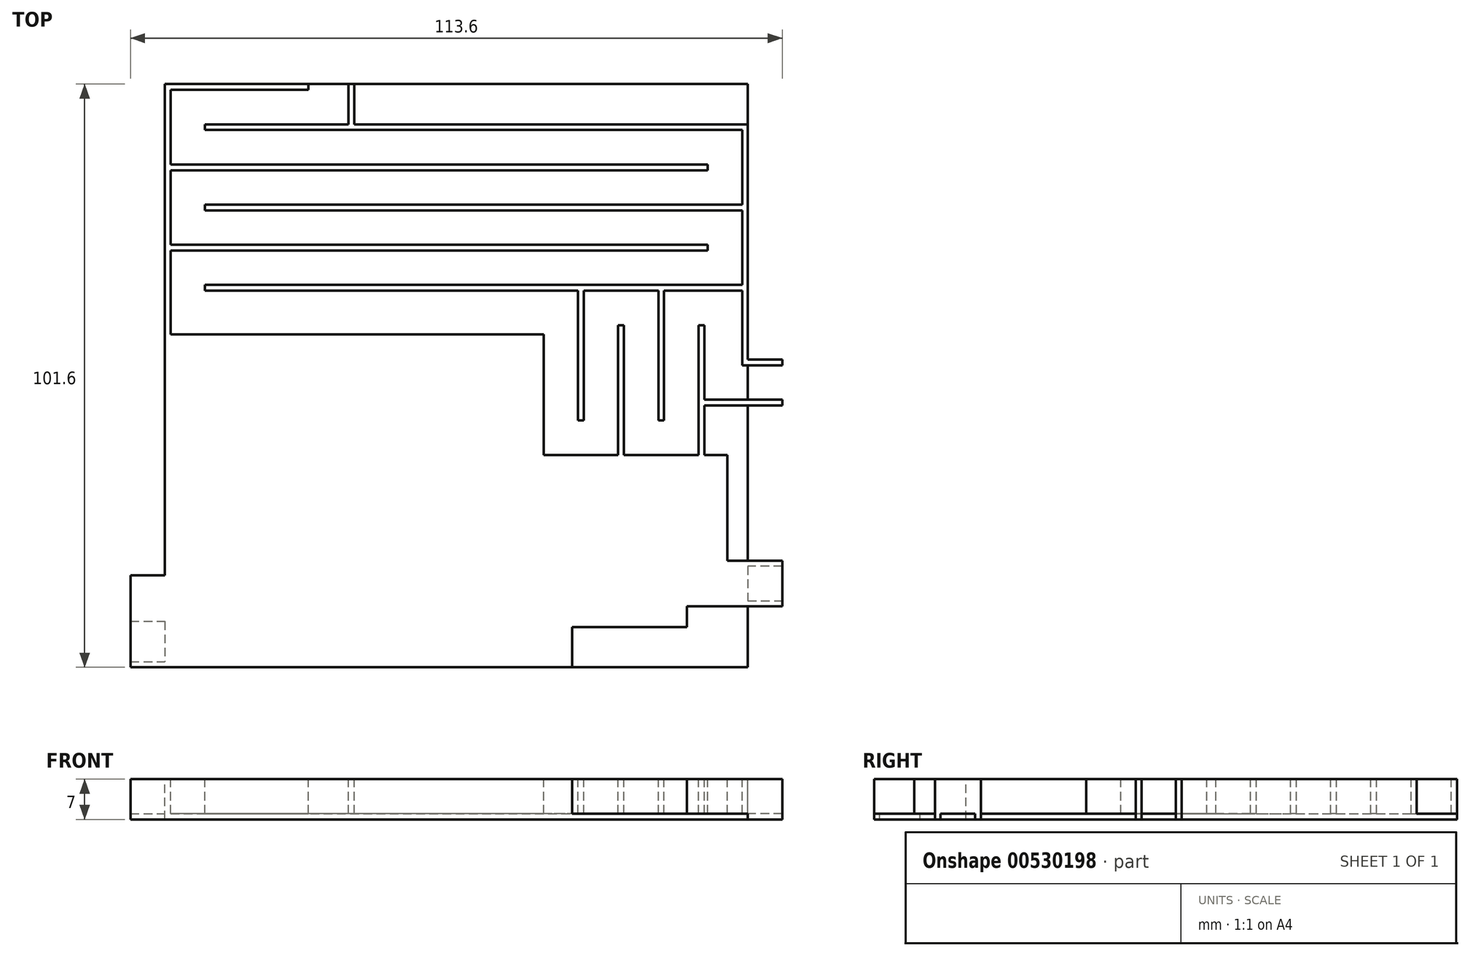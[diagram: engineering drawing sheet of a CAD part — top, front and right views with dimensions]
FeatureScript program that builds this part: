
annotation { "Feature Type Name" : "Feature", "Feature Type Description" : "" }
export const myFeature = defineFeature(function(context is Context, id is Id, definition is map)
    precondition{}
    {
        {
            var Q0;
            Q0=qCreatedBy(makeId("Top.planeOp"),FACE);
            var sketch = newSketch(context, id + "F0", { "sketchPlane" : qUnion([Q0])});
            skLineSegment(sketch, "E0.bottom", {"start": v(56.8, 50.8) * mm, "end": v(-56.8, 50.8) * mm});
            skLineSegment(sketch, "E0.top", {"start": v(56.8, -50.8) * mm, "end": v(-56.8, -50.8) * mm});
            skLineSegment(sketch, "E0.left", {"start": v(56.8, 50.8) * mm, "end": v(56.8, -50.8) * mm});
            skLineSegment(sketch, "E0.right", {"start": v(-56.8, 50.8) * mm, "end": v(-56.8, -50.8) * mm});
            skPoint(sketch, "E0.middle", {"position": v(0, 0) * mm});
            skSolve(sketch);
        }
        {
            var Q0;
            Q0=makeQuery(id+"F0.imprint","IMPRINT",FACE,{"disambiguationData":[TD([[makeQuery(id+"F0.imprint","IMPRINT",EDGE,{"derivedFrom":sQuery(id+"F0.wireOp",EDGE,"E0.bottom")}),1.0]])]});
            extrude(context, id + "F1", {"entities" : qUnion([Q0]), "depth" : 7 * mm, "offsetDistance" : 25.4 * mm});
        }
        {
            var Q0;
            Q0=makeQuery(id+"F1.opExtrude","CAP_FACE",FACE,{"disambiguationData":[OSD([sQuery(id+"F0.wireOp",EDGE,"E0.bottom"),sQuery(id+"F0.wireOp",EDGE,"E0.top"),sQuery(id+"F0.wireOp",EDGE,"E0.left"),sQuery(id+"F0.wireOp",EDGE,"E0.right")])],"isStart":false});
            var sketch = newSketch(context, id + "F2", { "sketchPlane" : qUnion([Q0])});
            skPoint(sketch, "E1", {"position": v(-56.8, -42.8) * mm});
            skPoint(sketch, "E2", {"position": v(-10.8, -41.8) * mm});
            skLineSegment(sketch, "E3.bottom", {"start": v(-56.8, -42.8) * mm, "end": v(-10.8, -42.8) * mm});
            skLineSegment(sketch, "E3.top", {"start": v(-56.8, -41.8) * mm, "end": v(-10.8, -41.8) * mm});
            skLineSegment(sketch, "E3.left", {"start": v(-56.8, -42.8) * mm, "end": v(-56.8, -41.8) * mm});
            skLineSegment(sketch, "E3.right", {"start": v(-10.8, -42.8) * mm, "end": v(-10.8, -41.8) * mm});
            skPoint(sketch, "E4", {"position": v(-56.8, -35.8) * mm});
            skPoint(sketch, "E5", {"position": v(-49.8, -34.8) * mm});
            skLineSegment(sketch, "E6.bottom", {"start": v(-56.8, -35.8) * mm, "end": v(-49.8, -35.8) * mm});
            skLineSegment(sketch, "E6.top", {"start": v(-56.8, -34.8) * mm, "end": v(-49.8, -34.8) * mm});
            skLineSegment(sketch, "E6.left", {"start": v(-56.8, -35.8) * mm, "end": v(-56.8, -34.8) * mm});
            skLineSegment(sketch, "E6.right", {"start": v(-49.8, -35.8) * mm, "end": v(-49.8, -34.8) * mm});
            skPoint(sketch, "E7", {"position": v(-50.8, 7.2) * mm});
            skLineSegment(sketch, "E8.bottom", {"start": v(-50.8, 7.2) * mm, "end": v(-49.8, 7.2) * mm});
            skLineSegment(sketch, "E8.top", {"start": v(-50.8, -34.8) * mm, "end": v(-49.8, -34.8) * mm});
            skLineSegment(sketch, "E8.left", {"start": v(-50.8, 7.2) * mm, "end": v(-50.8, -34.8) * mm});
            skLineSegment(sketch, "E8.right", {"start": v(-49.8, 7.2) * mm, "end": v(-49.8, -34.8) * mm});
            skPoint(sketch, "E9", {"position": v(-11.8, -13.8) * mm});
            skLineSegment(sketch, "E10.bottom", {"start": v(-11.8, -13.8) * mm, "end": v(-10.8, -13.8) * mm});
            skLineSegment(sketch, "E10.top", {"start": v(-11.8, -41.8) * mm, "end": v(-10.8, -41.8) * mm});
            skLineSegment(sketch, "E10.left", {"start": v(-11.8, -13.8) * mm, "end": v(-11.8, -41.8) * mm});
            skLineSegment(sketch, "E10.right", {"start": v(-10.8, -13.8) * mm, "end": v(-10.8, -41.8) * mm});
            skPoint(sketch, "E11", {"position": v(-17.8, -35.8) * mm});
            skLineSegment(sketch, "E12.bottom", {"start": v(-17.8, -35.8) * mm, "end": v(-49.8, -35.8) * mm});
            skLineSegment(sketch, "E12.top", {"start": v(-17.8, -34.8) * mm, "end": v(-49.8, -34.8) * mm});
            skLineSegment(sketch, "E12.left", {"start": v(-17.8, -35.8) * mm, "end": v(-17.8, -34.8) * mm});
            skPoint(sketch, "E13", {"position": v(-43.8, -28.8) * mm});
            skPoint(sketch, "E14", {"position": v(-11.8, -27.8) * mm});
            skLineSegment(sketch, "E15.bottom", {"start": v(-43.8, -28.8) * mm, "end": v(-11.8, -28.8) * mm});
            skLineSegment(sketch, "E15.top", {"start": v(-43.8, -27.8) * mm, "end": v(-11.8, -27.8) * mm});
            skLineSegment(sketch, "E15.left", {"start": v(-43.8, -28.8) * mm, "end": v(-43.8, -27.8) * mm});
            skLineSegment(sketch, "E15.right", {"start": v(-11.8, -28.8) * mm, "end": v(-11.8, -27.8) * mm});
            skPoint(sketch, "E16", {"position": v(-17.8, -21.8) * mm});
            skPoint(sketch, "E17", {"position": v(-49.8, -20.8) * mm});
            skLineSegment(sketch, "E18.bottom", {"start": v(-49.8, -20.8) * mm, "end": v(-17.8, -20.8) * mm});
            skLineSegment(sketch, "E18.top", {"start": v(-49.8, -21.8) * mm, "end": v(-17.8, -21.8) * mm});
            skLineSegment(sketch, "E18.left", {"start": v(-49.8, -20.8) * mm, "end": v(-49.8, -21.8) * mm});
            skLineSegment(sketch, "E18.right", {"start": v(-17.8, -20.8) * mm, "end": v(-17.8, -21.8) * mm});
            skPoint(sketch, "E19", {"position": v(-43.8, -14.8) * mm});
            skLineSegment(sketch, "E20.bottom", {"start": v(-43.8, -14.8) * mm, "end": v(-11.8, -14.8) * mm});
            skLineSegment(sketch, "E20.top", {"start": v(-43.8, -13.8) * mm, "end": v(-11.8, -13.8) * mm});
            skLineSegment(sketch, "E20.left", {"start": v(-43.8, -14.8) * mm, "end": v(-43.8, -13.8) * mm});
            skLineSegment(sketch, "E20.right", {"start": v(-11.8, -14.8) * mm, "end": v(-11.8, -13.8) * mm});
            skPoint(sketch, "E21", {"position": v(-17.8, -7.8) * mm});
            skPoint(sketch, "E22", {"position": v(-49.8, -6.8) * mm});
            skLineSegment(sketch, "E23.bottom", {"start": v(-49.8, -6.8) * mm, "end": v(-17.8, -6.8) * mm});
            skLineSegment(sketch, "E23.top", {"start": v(-49.8, -7.8) * mm, "end": v(-17.8, -7.8) * mm});
            skLineSegment(sketch, "E23.left", {"start": v(-49.8, -6.8) * mm, "end": v(-49.8, -7.8) * mm});
            skLineSegment(sketch, "E23.right", {"start": v(-17.8, -6.8) * mm, "end": v(-17.8, -7.8) * mm});
            skPoint(sketch, "E24", {"position": v(-10.8, -7.8) * mm});
            skPoint(sketch, "E25", {"position": v(-11.8, 0.2) * mm});
            skLineSegment(sketch, "E26.bottom", {"start": v(-11.8, 0.2) * mm, "end": v(-10.8, 0.2) * mm});
            skLineSegment(sketch, "E26.top", {"start": v(-11.8, -7.8) * mm, "end": v(-10.8, -7.8) * mm});
            skPoint(sketch, "E27", {"position": v(-43.8, -0.8) * mm});
            skLineSegment(sketch, "E28.bottom", {"start": v(-43.8, -0.8) * mm, "end": v(-10.8, -0.8) * mm});
            skLineSegment(sketch, "E28.top", {"start": v(-43.8, 0.2) * mm, "end": v(-10.8, 0.2) * mm});
            skLineSegment(sketch, "E28.left", {"start": v(-43.8, -0.8) * mm, "end": v(-43.8, 0.2) * mm});
            skLineSegment(sketch, "E28.right", {"start": v(-10.8, -0.8) * mm, "end": v(-10.8, 0.2) * mm});
            skPoint(sketch, "E29", {"position": v(14.2, 6.2) * mm});
            skLineSegment(sketch, "E30.bottom", {"start": v(-49.8, 7.2) * mm, "end": v(14.2, 7.2) * mm});
            skLineSegment(sketch, "E30.top", {"start": v(-49.8, 6.2) * mm, "end": v(14.2, 6.2) * mm});
            skLineSegment(sketch, "E30.left", {"start": v(-49.8, 7.2) * mm, "end": v(-49.8, 6.2) * mm});
            skLineSegment(sketch, "E30.right", {"start": v(14.2, 7.2) * mm, "end": v(14.2, 6.2) * mm});
            skPoint(sketch, "E31", {"position": v(8.2, 0.2) * mm});
            skLineSegment(sketch, "E32.bottom", {"start": v(8.2, 0.2) * mm, "end": v(-10.8, 0.2) * mm});
            skLineSegment(sketch, "E32.top", {"start": v(8.2, -0.8) * mm, "end": v(-10.8, -0.8) * mm});
            skLineSegment(sketch, "E32.left", {"start": v(8.2, 0.2) * mm, "end": v(8.2, -0.8) * mm});
            skLineSegment(sketch, "E32.right", {"start": v(-10.8, 0.2) * mm, "end": v(-10.8, -0.8) * mm});
            skPoint(sketch, "E33", {"position": v(15.2, -14.8) * mm});
            skLineSegment(sketch, "E34.bottom", {"start": v(15.2, -14.8) * mm, "end": v(14.2, -14.8) * mm});
            skLineSegment(sketch, "E34.top", {"start": v(15.2, 7.2) * mm, "end": v(14.2, 7.2) * mm});
            skLineSegment(sketch, "E34.left", {"start": v(15.2, -14.8) * mm, "end": v(15.2, 7.2) * mm});
            skLineSegment(sketch, "E34.right", {"start": v(14.2, -14.8) * mm, "end": v(14.2, 7.2) * mm});
            skPoint(sketch, "E35", {"position": v(7.2, -21.8) * mm});
            skLineSegment(sketch, "E36.bottom", {"start": v(7.2, -21.8) * mm, "end": v(8.2, -21.8) * mm});
            skLineSegment(sketch, "E36.top", {"start": v(7.2, 0.2) * mm, "end": v(8.2, 0.2) * mm});
            skLineSegment(sketch, "E36.left", {"start": v(7.2, -21.8) * mm, "end": v(7.2, 0.2) * mm});
            skLineSegment(sketch, "E36.right", {"start": v(8.2, -21.8) * mm, "end": v(8.2, 0.2) * mm});
            skPoint(sketch, "E37", {"position": v(39.2, -13.8) * mm});
            skLineSegment(sketch, "E38.bottom", {"start": v(15.2, -14.8) * mm, "end": v(39.2, -14.8) * mm});
            skLineSegment(sketch, "E38.top", {"start": v(15.2, -13.8) * mm, "end": v(39.2, -13.8) * mm});
            skLineSegment(sketch, "E38.left", {"start": v(15.2, -14.8) * mm, "end": v(15.2, -13.8) * mm});
            skLineSegment(sketch, "E38.right", {"start": v(39.2, -14.8) * mm, "end": v(39.2, -13.8) * mm});
            skPoint(sketch, "E39", {"position": v(40.2, -43.8) * mm});
            skLineSegment(sketch, "E40.bottom", {"start": v(40.2, -43.8) * mm, "end": v(39.2, -43.8) * mm});
            skLineSegment(sketch, "E40.top", {"start": v(40.2, -14.8) * mm, "end": v(39.2, -14.8) * mm});
            skLineSegment(sketch, "E40.left", {"start": v(40.2, -43.8) * mm, "end": v(40.2, -14.8) * mm});
            skLineSegment(sketch, "E40.right", {"start": v(39.2, -43.8) * mm, "end": v(39.2, -14.8) * mm});
            skLineSegment(sketch, "E41.top", {"start": v(40.2, -13.8) * mm, "end": v(39.2, -13.8) * mm});
            skLineSegment(sketch, "E41.left", {"start": v(40.2, -43.8) * mm, "end": v(40.2, -13.8) * mm});
            skLineSegment(sketch, "E41.right", {"start": v(39.2, -43.8) * mm, "end": v(39.2, -13.8) * mm});
            skPoint(sketch, "E42", {"position": v(20.2, -42.8) * mm});
            skLineSegment(sketch, "E43.bottom", {"start": v(20.2, -42.8) * mm, "end": v(40.2, -42.8) * mm});
            skLineSegment(sketch, "E43.top", {"start": v(20.2, -43.8) * mm, "end": v(40.2, -43.8) * mm});
            skLineSegment(sketch, "E43.left", {"start": v(20.2, -42.8) * mm, "end": v(20.2, -43.8) * mm});
            skLineSegment(sketch, "E43.right", {"start": v(40.2, -42.8) * mm, "end": v(40.2, -43.8) * mm});
            skPoint(sketch, "E44", {"position": v(19.2, -50.8) * mm});
            skLineSegment(sketch, "E45.bottom", {"start": v(19.2, -50.8) * mm, "end": v(20.2, -50.8) * mm});
            skLineSegment(sketch, "E45.top", {"start": v(19.2, -42.8) * mm, "end": v(20.2, -42.8) * mm});
            skLineSegment(sketch, "E45.left", {"start": v(19.2, -50.8) * mm, "end": v(19.2, -42.8) * mm});
            skLineSegment(sketch, "E45.right", {"start": v(20.2, -50.8) * mm, "end": v(20.2, -42.8) * mm});
            skPoint(sketch, "E46", {"position": v(33.2, -20.8) * mm});
            skLineSegment(sketch, "E47.bottom", {"start": v(33.2, -20.8) * mm, "end": v(8.2, -20.8) * mm});
            skLineSegment(sketch, "E47.top", {"start": v(33.2, -21.8) * mm, "end": v(8.2, -21.8) * mm});
            skLineSegment(sketch, "E47.left", {"start": v(33.2, -20.8) * mm, "end": v(33.2, -21.8) * mm});
            skLineSegment(sketch, "E47.right", {"start": v(8.2, -20.8) * mm, "end": v(8.2, -21.8) * mm});
            skPoint(sketch, "E48", {"position": v(32.2, -36.8) * mm});
            skLineSegment(sketch, "E49.bottom", {"start": v(32.2, -36.8) * mm, "end": v(33.2, -36.8) * mm});
            skLineSegment(sketch, "E49.top", {"start": v(32.2, -21.8) * mm, "end": v(33.2, -21.8) * mm});
            skLineSegment(sketch, "E49.left", {"start": v(32.2, -36.8) * mm, "end": v(32.2, -21.8) * mm});
            skLineSegment(sketch, "E49.right", {"start": v(33.2, -36.8) * mm, "end": v(33.2, -21.8) * mm});
            skPoint(sketch, "E50", {"position": v(13.2, -35.8) * mm});
            skLineSegment(sketch, "E51.bottom", {"start": v(13.2, -35.8) * mm, "end": v(32.2, -35.8) * mm});
            skLineSegment(sketch, "E51.top", {"start": v(13.2, -36.8) * mm, "end": v(32.2, -36.8) * mm});
            skLineSegment(sketch, "E51.left", {"start": v(13.2, -35.8) * mm, "end": v(13.2, -36.8) * mm});
            skLineSegment(sketch, "E51.right", {"start": v(32.2, -35.8) * mm, "end": v(32.2, -36.8) * mm});
            skPoint(sketch, "E52", {"position": v(12.2, -50.8) * mm});
            skLineSegment(sketch, "E53.bottom", {"start": v(12.2, -50.8) * mm, "end": v(13.2, -50.8) * mm});
            skLineSegment(sketch, "E53.top", {"start": v(12.2, -35.8) * mm, "end": v(13.2, -35.8) * mm});
            skLineSegment(sketch, "E53.left", {"start": v(12.2, -50.8) * mm, "end": v(12.2, -35.8) * mm});
            skLineSegment(sketch, "E53.right", {"start": v(13.2, -50.8) * mm, "end": v(13.2, -35.8) * mm});
            skLineSegment(sketch, "E54.bottom", {"start": v(-10.8, -7.8) * mm, "end": v(-11.8, -7.8) * mm});
            skLineSegment(sketch, "E54.top", {"start": v(-10.8, -13.8) * mm, "end": v(-11.8, -13.8) * mm});
            skLineSegment(sketch, "E54.left", {"start": v(-10.8, -7.8) * mm, "end": v(-10.8, -13.8) * mm});
            skLineSegment(sketch, "E54.right", {"start": v(-11.8, -7.8) * mm, "end": v(-11.8, -13.8) * mm});
            skPoint(sketch, "E55", {"position": v(1.2, -6.8) * mm});
            skLineSegment(sketch, "E56.bottom", {"start": v(1.2, -6.8) * mm, "end": v(-11.8, -6.8) * mm});
            skLineSegment(sketch, "E56.top", {"start": v(1.2, -7.8) * mm, "end": v(-11.8, -7.8) * mm});
            skLineSegment(sketch, "E56.left", {"start": v(1.2, -6.8) * mm, "end": v(1.2, -7.8) * mm});
            skLineSegment(sketch, "E56.right", {"start": v(-11.8, -6.8) * mm, "end": v(-11.8, -7.8) * mm});
            skPoint(sketch, "E57", {"position": v(-4.8, -13.8) * mm});
            skPoint(sketch, "E58", {"position": v(7.2, -14.8) * mm});
            skLineSegment(sketch, "E59.bottom", {"start": v(-4.8, -13.8) * mm, "end": v(7.2, -13.8) * mm});
            skLineSegment(sketch, "E59.top", {"start": v(-4.8, -14.8) * mm, "end": v(7.2, -14.8) * mm});
            skLineSegment(sketch, "E59.left", {"start": v(-4.8, -13.8) * mm, "end": v(-4.8, -14.8) * mm});
            skLineSegment(sketch, "E59.right", {"start": v(7.2, -13.8) * mm, "end": v(7.2, -14.8) * mm});
            skPoint(sketch, "E60", {"position": v(-10.8, -20.8) * mm});
            skPoint(sketch, "E61", {"position": v(1.2, -21.8) * mm});
            skLineSegment(sketch, "E62.bottom", {"start": v(-10.8, -20.8) * mm, "end": v(1.2, -20.8) * mm});
            skLineSegment(sketch, "E62.top", {"start": v(-10.8, -21.8) * mm, "end": v(1.2, -21.8) * mm});
            skLineSegment(sketch, "E62.left", {"start": v(-10.8, -20.8) * mm, "end": v(-10.8, -21.8) * mm});
            skLineSegment(sketch, "E62.right", {"start": v(1.2, -20.8) * mm, "end": v(1.2, -21.8) * mm});
            skPoint(sketch, "E63", {"position": v(26.2, -28.8) * mm});
            skLineSegment(sketch, "E64.bottom", {"start": v(26.2, -28.8) * mm, "end": v(-11.8, -28.8) * mm});
            skLineSegment(sketch, "E64.top", {"start": v(26.2, -27.8) * mm, "end": v(-11.8, -27.8) * mm});
            skLineSegment(sketch, "E64.left", {"start": v(26.2, -28.8) * mm, "end": v(26.2, -27.8) * mm});
            skPoint(sketch, "E65", {"position": v(-4.8, -36.8) * mm});
            skLineSegment(sketch, "E66.bottom", {"start": v(-4.8, -36.8) * mm, "end": v(13.2, -36.8) * mm});
            skLineSegment(sketch, "E66.top", {"start": v(-4.8, -35.8) * mm, "end": v(13.2, -35.8) * mm});
            skLineSegment(sketch, "E66.left", {"start": v(-4.8, -36.8) * mm, "end": v(-4.8, -35.8) * mm});
            skLineSegment(sketch, "E66.right", {"start": v(13.2, -36.8) * mm, "end": v(13.2, -35.8) * mm});
            skPoint(sketch, "E67", {"position": v(6.2, -41.8) * mm});
            skPoint(sketch, "E68", {"position": v(5.2, -50.8) * mm});
            skLineSegment(sketch, "E69.bottom", {"start": v(6.2, -41.8) * mm, "end": v(5.2, -41.8) * mm});
            skLineSegment(sketch, "E69.top", {"start": v(6.2, -50.8) * mm, "end": v(5.2, -50.8) * mm});
            skLineSegment(sketch, "E69.left", {"start": v(6.2, -41.8) * mm, "end": v(6.2, -50.8) * mm});
            skLineSegment(sketch, "E69.right", {"start": v(5.2, -41.8) * mm, "end": v(5.2, -50.8) * mm});
            skPoint(sketch, "E70", {"position": v(-0.8, -42.8) * mm});
            skLineSegment(sketch, "E71.bottom", {"start": v(-0.8, -42.8) * mm, "end": v(-10.8, -42.8) * mm});
            skLineSegment(sketch, "E71.top", {"start": v(-0.8, -41.8) * mm, "end": v(-10.8, -41.8) * mm});
            skLineSegment(sketch, "E71.left", {"start": v(-0.8, -42.8) * mm, "end": v(-0.8, -41.8) * mm});
            skPoint(sketch, "E72", {"position": v(-0.8, -50.8) * mm});
            skPoint(sketch, "E72.positionSnap0", {"position": v(0, -50.8) * mm});
            skPoint(sketch, "E73", {"position": v(-1.8, -48.8) * mm});
            skLineSegment(sketch, "E74.bottom", {"start": v(-1.8, -48.8) * mm, "end": v(-0.8, -48.8) * mm});
            skLineSegment(sketch, "E74.top", {"start": v(-1.8, -50.8) * mm, "end": v(-0.8, -50.8) * mm});
            skLineSegment(sketch, "E74.left", {"start": v(-1.8, -48.8) * mm, "end": v(-1.8, -50.8) * mm});
            skLineSegment(sketch, "E74.right", {"start": v(-0.8, -48.8) * mm, "end": v(-0.8, -50.8) * mm});
            skPoint(sketch, "E75", {"position": v(-56.8, -49.8) * mm});
            skLineSegment(sketch, "E76.bottom", {"start": v(-56.8, -49.8) * mm, "end": v(-1.8, -49.8) * mm});
            skLineSegment(sketch, "E76.top", {"start": v(-56.8, -48.8) * mm, "end": v(-1.8, -48.8) * mm});
            skLineSegment(sketch, "E76.left", {"start": v(-56.8, -49.8) * mm, "end": v(-56.8, -48.8) * mm});
            skLineSegment(sketch, "E76.right", {"start": v(-1.8, -49.8) * mm, "end": v(-1.8, -48.8) * mm});
            skSolve(sketch);
        }
        {
            var Q0;
            {var subQ14=sQuery(id+"F2.wireOp",EDGE,"E3.bottom");Q0=makeQuery(id+"F2.imprint","IMPRINT",FACE,{"disambiguationData":[TD([[makeQuery(id+"F2.imprint","IMPRINT",EDGE,{"derivedFrom":subQ14}),-1.0]])]});}
            var Q1;
            {var subQ0=sQuery(id+"F2.wireOp",EDGE,"E74.left");Q1=makeQuery(id+"F2.imprint","IMPRINT",FACE,{"disambiguationData":[TD([[makeQuery(id+"F2.imprint","IMPRINT",EDGE,{"derivedFrom":subQ0}),-1.0]])]});}
            extrude(context, id + "F3", {"entities" : qUnion([Q0, Q1]), "operationType" : NewBodyOperationType.REMOVE, "oppositeDirection" : true, "depth" : 6 * mm, "offsetDistance" : 25.4 * mm});
        }
        {
            var Q0;
            {var subQ9=sQuery(id+"F0.wireOp",EDGE,"E0.bottom");var subQ10=sQuery(id+"F0.wireOp",EDGE,"E0.right");var subQ11=sQuery(id+"F0.wireOp",EDGE,"E0.top");var subQ12=sQuery(id+"F0.wireOp",EDGE,"E0.left");Q0=makeQuery(id+"F3.boolean.opBoolean","SPLIT",FACE,{"disambiguationData":[TD([makeQuery(id+"F1.opExtrude","SWEPT_FACE",FACE,{"disambiguationData":[OSD([subQ9])]})])],"derivedFrom":makeQuery(id+"F1.opExtrude","CAP_FACE",FACE,{"disambiguationData":[OSD([subQ9,subQ11,subQ12,subQ10])],"isStart":false})});}
            var sketch = newSketch(context, id + "F4", { "sketchPlane" : qUnion([Q0])});
            skPoint(sketch, "E77", {"position": v(56.8, -43.8) * mm});
            skLineSegment(sketch, "E78.left", {"start": v(19.2, -42.8) * mm, "end": v(19.2, -43.8) * mm});
            skLineSegment(sketch, "E78.right", {"start": v(56.8, -42.8) * mm, "end": v(56.8, -43.8) * mm});
            skPoint(sketch, "E79", {"position": v(20.2, -50.8) * mm});
            skLineSegment(sketch, "E80.bottom", {"start": v(20.2, -50.8) * mm, "end": v(19.2, -50.8) * mm});
            skLineSegment(sketch, "E80.top", {"start": v(20.2, -43.8) * mm, "end": v(19.2, -43.8) * mm});
            skLineSegment(sketch, "E80.left", {"start": v(20.2, -50.8) * mm, "end": v(20.2, -43.8) * mm});
            skLineSegment(sketch, "E80.right", {"start": v(19.2, -50.8) * mm, "end": v(19.2, -43.8) * mm});
            skPoint(sketch, "E81", {"position": v(56.8, -36.8) * mm});
            skPoint(sketch, "E82", {"position": v(39.2, -35.8) * mm});
            skLineSegment(sketch, "E83.left", {"start": v(39.2, -35.8) * mm, "end": v(39.2, -36.8) * mm});
            skLineSegment(sketch, "E83.right", {"start": v(56.8, -35.8) * mm, "end": v(56.8, -36.8) * mm});
            skPoint(sketch, "E84", {"position": v(56.8, -40.2) * mm});
            skPoint(sketch, "E85", {"position": v(39.2, -39.2) * mm});
            skLineSegment(sketch, "E86.bottom", {"start": v(39.2, -39.2) * mm, "end": v(56.8, -39.2) * mm});
            skLineSegment(sketch, "E86.top", {"start": v(39.2, -40.2) * mm, "end": v(56.8, -40.2) * mm});
            skLineSegment(sketch, "E86.left", {"start": v(39.2, -39.2) * mm, "end": v(39.2, -40.2) * mm});
            skLineSegment(sketch, "E86.right", {"start": v(56.8, -39.2) * mm, "end": v(56.8, -40.2) * mm});
            skPoint(sketch, "E87", {"position": v(40.2, -43.8) * mm});
            skLineSegment(sketch, "E88.bottom", {"start": v(40.2, -43.8) * mm, "end": v(19.2, -43.8) * mm});
            skLineSegment(sketch, "E88.top", {"start": v(40.2, -42.8) * mm, "end": v(19.2, -42.8) * mm});
            skLineSegment(sketch, "E88.left", {"start": v(40.2, -43.8) * mm, "end": v(40.2, -42.8) * mm});
            skLineSegment(sketch, "E88.right", {"start": v(19.2, -43.8) * mm, "end": v(19.2, -42.8) * mm});
            skLineSegment(sketch, "E89.bottom", {"start": v(40.2, -43.8) * mm, "end": v(39.2, -43.8) * mm});
            skLineSegment(sketch, "E89.top", {"start": v(40.2, -39.2) * mm, "end": v(39.2, -39.2) * mm});
            skLineSegment(sketch, "E89.left", {"start": v(40.2, -43.8) * mm, "end": v(40.2, -39.2) * mm});
            skLineSegment(sketch, "E89.right", {"start": v(39.2, -43.8) * mm, "end": v(39.2, -39.2) * mm});
            skPoint(sketch, "E90", {"position": v(56.8, -33.2) * mm});
            skPoint(sketch, "E91", {"position": v(47.2, -13.8) * mm});
            skLineSegment(sketch, "E92.bottom", {"start": v(47.2, -13.8) * mm, "end": v(14.2, -13.8) * mm});
            skLineSegment(sketch, "E92.top", {"start": v(47.2, -14.8) * mm, "end": v(14.2, -14.8) * mm});
            skLineSegment(sketch, "E92.left", {"start": v(47.2, -13.8) * mm, "end": v(47.2, -14.8) * mm});
            skLineSegment(sketch, "E92.right", {"start": v(14.2, -13.8) * mm, "end": v(14.2, -14.8) * mm});
            skPoint(sketch, "E93", {"position": v(40.2, -20.8) * mm});
            skLineSegment(sketch, "E94.bottom", {"start": v(40.2, -20.8) * mm, "end": v(39.2, -20.8) * mm});
            skLineSegment(sketch, "E94.left", {"start": v(40.2, -20.8) * mm, "end": v(40.2, -39.2) * mm});
            skLineSegment(sketch, "E94.right", {"start": v(39.2, -20.8) * mm, "end": v(39.2, -39.2) * mm});
            skPoint(sketch, "E95", {"position": v(46.2, -32.2) * mm});
            skLineSegment(sketch, "E96.bottom", {"start": v(46.2, -32.2) * mm, "end": v(47.2, -32.2) * mm});
            skLineSegment(sketch, "E96.top", {"start": v(46.2, -14.8) * mm, "end": v(47.2, -14.8) * mm});
            skLineSegment(sketch, "E96.left", {"start": v(46.2, -32.2) * mm, "end": v(46.2, -14.8) * mm});
            skLineSegment(sketch, "E96.right", {"start": v(47.2, -32.2) * mm, "end": v(47.2, -14.8) * mm});
            skLineSegment(sketch, "E97.bottom", {"start": v(56.8, -33.2) * mm, "end": v(46.2, -33.2) * mm});
            skLineSegment(sketch, "E97.top", {"start": v(56.8, -32.2) * mm, "end": v(46.2, -32.2) * mm});
            skLineSegment(sketch, "E97.left", {"start": v(56.8, -33.2) * mm, "end": v(56.8, -32.2) * mm});
            skLineSegment(sketch, "E97.right", {"start": v(46.2, -33.2) * mm, "end": v(46.2, -32.2) * mm});
            skPoint(sketch, "E98", {"position": v(56.8, -50.8) * mm});
            skSolve(sketch);
        }
        {
            var Q0;
            {var subQ12=sQuery(id+"F4.wireOp",EDGE,"E78.right");Q0=makeQuery(id+"F4.imprint","IMPRINT",FACE,{"disambiguationData":[TD([[makeQuery(id+"F4.imprint","IMPRINT",EDGE,{"derivedFrom":subQ12}),-1.0]])]});}
            var Q1;
            {var subQ7=sQuery(id+"F4.wireOp",EDGE,"E83.right");Q1=makeQuery(id+"F4.imprint","IMPRINT",FACE,{"disambiguationData":[TD([[makeQuery(id+"F4.imprint","IMPRINT",EDGE,{"derivedFrom":subQ7}),-1.0]])]});}
            extrude(context, id + "F5", {"entities" : qUnion([Q0, Q1]), "operationType" : NewBodyOperationType.REMOVE, "oppositeDirection" : true, "depth" : 6 * mm, "offsetDistance" : 25.4 * mm});
        }
        {
            var Q0;
            {var subQ16=sQuery(id+"F0.wireOp",EDGE,"E0.bottom");var subQ17=makeQuery(id+"F1.opExtrude","SWEPT_FACE",FACE,{"disambiguationData":[OSD([subQ16])]});var subQ18=sQuery(id+"F0.wireOp",EDGE,"E0.right");var subQ20=sQuery(id+"F0.wireOp",EDGE,"E0.left");var subQ30=sQuery(id+"F0.wireOp",EDGE,"E0.top");Q0=makeQuery(id+"F5.boolean.opBoolean","SPLIT",FACE,{"disambiguationData":[TD([subQ17])],"derivedFrom":makeQuery(id+"F3.boolean.opBoolean","SPLIT",FACE,{"disambiguationData":[TD([subQ17])],"derivedFrom":makeQuery(id+"F1.opExtrude","CAP_FACE",FACE,{"disambiguationData":[OSD([subQ16,subQ30,subQ20,subQ18])],"isStart":false})})});}
            var sketch = newSketch(context, id + "F6", { "sketchPlane" : qUnion([Q0])});
            skPoint(sketch, "E99", {"position": v(-25.8, 50.8) * mm});
            skPoint(sketch, "E100", {"position": v(-18.8, 50.8) * mm});
            skPoint(sketch, "E101", {"position": v(-17.8, 43.8) * mm});
            skLineSegment(sketch, "E102.bottom", {"start": v(-18.8, 50.8) * mm, "end": v(-17.8, 50.8) * mm});
            skLineSegment(sketch, "E102.top", {"start": v(-18.8, 43.8) * mm, "end": v(-17.8, 43.8) * mm});
            skLineSegment(sketch, "E102.left", {"start": v(-18.8, 50.8) * mm, "end": v(-18.8, 43.8) * mm});
            skLineSegment(sketch, "E102.right", {"start": v(-17.8, 50.8) * mm, "end": v(-17.8, 43.8) * mm});
            skPoint(sketch, "E103", {"position": v(-50.8, 49.8) * mm});
            skLineSegment(sketch, "E104.bottom", {"start": v(-50.8, 49.8) * mm, "end": v(-25.8, 49.8) * mm});
            skLineSegment(sketch, "E104.top", {"start": v(-50.8, 50.8) * mm, "end": v(-25.8, 50.8) * mm});
            skLineSegment(sketch, "E104.left", {"start": v(-50.8, 49.8) * mm, "end": v(-50.8, 50.8) * mm});
            skLineSegment(sketch, "E104.right", {"start": v(-25.8, 49.8) * mm, "end": v(-25.8, 50.8) * mm});
            skPoint(sketch, "E105", {"position": v(-49.8, 35.8) * mm});
            skLineSegment(sketch, "E106.bottom", {"start": v(-49.8, 35.8) * mm, "end": v(-50.8, 35.8) * mm});
            skLineSegment(sketch, "E106.top", {"start": v(-49.8, 49.8) * mm, "end": v(-50.8, 49.8) * mm});
            skLineSegment(sketch, "E106.left", {"start": v(-49.8, 35.8) * mm, "end": v(-49.8, 49.8) * mm});
            skLineSegment(sketch, "E106.right", {"start": v(-50.8, 35.8) * mm, "end": v(-50.8, 49.8) * mm});
            skPoint(sketch, "E107", {"position": v(-43.8, 42.8) * mm});
            skLineSegment(sketch, "E108.bottom", {"start": v(-43.8, 42.8) * mm, "end": v(-17.8, 42.8) * mm});
            skLineSegment(sketch, "E108.top", {"start": v(-43.8, 43.8) * mm, "end": v(-17.8, 43.8) * mm});
            skLineSegment(sketch, "E108.left", {"start": v(-43.8, 42.8) * mm, "end": v(-43.8, 43.8) * mm});
            skLineSegment(sketch, "E108.right", {"start": v(-17.8, 42.8) * mm, "end": v(-17.8, 43.8) * mm});
            skPoint(sketch, "E109", {"position": v(50.8, 42.8) * mm});
            skLineSegment(sketch, "E110.bottom", {"start": v(-17.8, 43.8) * mm, "end": v(50.8, 43.8) * mm});
            skLineSegment(sketch, "E110.top", {"start": v(-17.8, 42.8) * mm, "end": v(50.8, 42.8) * mm});
            skLineSegment(sketch, "E110.left", {"start": v(-17.8, 43.8) * mm, "end": v(-17.8, 42.8) * mm});
            skLineSegment(sketch, "E110.right", {"start": v(50.8, 43.8) * mm, "end": v(50.8, 42.8) * mm});
            skPoint(sketch, "E111", {"position": v(49.8, 28.8) * mm});
            skLineSegment(sketch, "E112.bottom", {"start": v(49.8, 28.8) * mm, "end": v(50.8, 28.8) * mm});
            skLineSegment(sketch, "E112.top", {"start": v(49.8, 43.8) * mm, "end": v(50.8, 43.8) * mm});
            skLineSegment(sketch, "E112.left", {"start": v(49.8, 28.8) * mm, "end": v(49.8, 43.8) * mm});
            skLineSegment(sketch, "E112.right", {"start": v(50.8, 28.8) * mm, "end": v(50.8, 43.8) * mm});
            skPoint(sketch, "E113", {"position": v(43.8, 36.8) * mm});
            skLineSegment(sketch, "E114.bottom", {"start": v(43.8, 36.8) * mm, "end": v(-49.8, 36.8) * mm});
            skLineSegment(sketch, "E114.top", {"start": v(43.8, 35.8) * mm, "end": v(-49.8, 35.8) * mm});
            skLineSegment(sketch, "E114.left", {"start": v(43.8, 36.8) * mm, "end": v(43.8, 35.8) * mm});
            skLineSegment(sketch, "E114.right", {"start": v(-49.8, 36.8) * mm, "end": v(-49.8, 35.8) * mm});
            skPoint(sketch, "E115", {"position": v(-50.8, 21.8) * mm});
            skLineSegment(sketch, "E116.bottom", {"start": v(-50.8, 21.8) * mm, "end": v(-49.8, 21.8) * mm});
            skLineSegment(sketch, "E116.top", {"start": v(-50.8, 35.8) * mm, "end": v(-49.8, 35.8) * mm});
            skLineSegment(sketch, "E116.left", {"start": v(-50.8, 21.8) * mm, "end": v(-50.8, 35.8) * mm});
            skLineSegment(sketch, "E116.right", {"start": v(-49.8, 21.8) * mm, "end": v(-49.8, 35.8) * mm});
            skPoint(sketch, "E117", {"position": v(-43.8, 29.8) * mm});
            skLineSegment(sketch, "E118.bottom", {"start": v(-43.8, 29.8) * mm, "end": v(50.8, 29.8) * mm});
            skLineSegment(sketch, "E118.top", {"start": v(-43.8, 28.8) * mm, "end": v(50.8, 28.8) * mm});
            skLineSegment(sketch, "E118.left", {"start": v(-43.8, 29.8) * mm, "end": v(-43.8, 28.8) * mm});
            skLineSegment(sketch, "E118.right", {"start": v(50.8, 29.8) * mm, "end": v(50.8, 28.8) * mm});
            skPoint(sketch, "E119", {"position": v(49.8, 14.8) * mm});
            skLineSegment(sketch, "E120.bottom", {"start": v(49.8, 14.8) * mm, "end": v(50.8, 14.8) * mm});
            skLineSegment(sketch, "E120.left", {"start": v(49.8, 14.8) * mm, "end": v(49.8, 28.8) * mm});
            skLineSegment(sketch, "E120.right", {"start": v(50.8, 14.8) * mm, "end": v(50.8, 28.8) * mm});
            skPoint(sketch, "E121", {"position": v(43.8, 22.8) * mm});
            skLineSegment(sketch, "E122.bottom", {"start": v(43.8, 22.8) * mm, "end": v(-49.8, 22.8) * mm});
            skLineSegment(sketch, "E122.top", {"start": v(43.8, 21.8) * mm, "end": v(-49.8, 21.8) * mm});
            skLineSegment(sketch, "E122.left", {"start": v(43.8, 22.8) * mm, "end": v(43.8, 21.8) * mm});
            skLineSegment(sketch, "E122.right", {"start": v(-49.8, 22.8) * mm, "end": v(-49.8, 21.8) * mm});
            skPoint(sketch, "E123", {"position": v(-49.8, 7.8) * mm});
            skLineSegment(sketch, "E124.bottom", {"start": v(-49.8, 7.8) * mm, "end": v(-50.8, 7.8) * mm});
            skLineSegment(sketch, "E124.top", {"start": v(-49.8, 21.8) * mm, "end": v(-50.8, 21.8) * mm});
            skLineSegment(sketch, "E124.left", {"start": v(-49.8, 7.8) * mm, "end": v(-49.8, 21.8) * mm});
            skLineSegment(sketch, "E124.right", {"start": v(-50.8, 7.8) * mm, "end": v(-50.8, 21.8) * mm});
            skPoint(sketch, "E125", {"position": v(-43.8, 15.8) * mm});
            skLineSegment(sketch, "E126.bottom", {"start": v(-43.8, 15.8) * mm, "end": v(49.8, 15.8) * mm});
            skLineSegment(sketch, "E126.top", {"start": v(-43.8, 14.8) * mm, "end": v(49.8, 14.8) * mm});
            skLineSegment(sketch, "E126.left", {"start": v(-43.8, 15.8) * mm, "end": v(-43.8, 14.8) * mm});
            skLineSegment(sketch, "E126.right", {"start": v(49.8, 15.8) * mm, "end": v(49.8, 14.8) * mm});
            skPoint(sketch, "E127", {"position": v(56.8, 2.8) * mm});
            skPoint(sketch, "E128", {"position": v(50.8, 1.8) * mm});
            skLineSegment(sketch, "E129.bottom", {"start": v(50.8, 1.8) * mm, "end": v(56.8, 1.8) * mm});
            skLineSegment(sketch, "E129.top", {"start": v(50.8, 2.8) * mm, "end": v(56.8, 2.8) * mm});
            skLineSegment(sketch, "E129.left", {"start": v(50.8, 1.8) * mm, "end": v(50.8, 2.8) * mm});
            skLineSegment(sketch, "E129.right", {"start": v(56.8, 1.8) * mm, "end": v(56.8, 2.8) * mm});
            skPoint(sketch, "E130", {"position": v(56.8, -4.2) * mm});
            skPoint(sketch, "E131", {"position": v(50.8, -5.2) * mm});
            skLineSegment(sketch, "E132.bottom", {"start": v(50.8, -5.2) * mm, "end": v(56.8, -5.2) * mm});
            skLineSegment(sketch, "E132.top", {"start": v(50.8, -4.2) * mm, "end": v(56.8, -4.2) * mm});
            skLineSegment(sketch, "E132.left", {"start": v(50.8, -5.2) * mm, "end": v(50.8, -4.2) * mm});
            skLineSegment(sketch, "E132.right", {"start": v(56.8, -5.2) * mm, "end": v(56.8, -4.2) * mm});
            skLineSegment(sketch, "E133.bottom", {"start": v(-56.8, -35.8) * mm, "end": v(-49.8, -35.8) * mm});
            skLineSegment(sketch, "E133.top", {"start": v(-56.8, -34.8) * mm, "end": v(-49.8, -34.8) * mm});
            skLineSegment(sketch, "E133.left", {"start": v(-56.8, -35.8) * mm, "end": v(-56.8, -34.8) * mm});
            skLineSegment(sketch, "E133.right", {"start": v(-49.8, -35.8) * mm, "end": v(-49.8, -34.8) * mm});
            skPoint(sketch, "E134", {"position": v(-50.8, 6.2) * mm});
            skLineSegment(sketch, "E135.bottom", {"start": v(-50.8, 6.2) * mm, "end": v(-49.8, 6.2) * mm});
            skLineSegment(sketch, "E135.top", {"start": v(-50.8, -34.8) * mm, "end": v(-49.8, -34.8) * mm});
            skLineSegment(sketch, "E135.left", {"start": v(-50.8, 6.2) * mm, "end": v(-50.8, -34.8) * mm});
            skLineSegment(sketch, "E135.right", {"start": v(-49.8, 6.2) * mm, "end": v(-49.8, -34.8) * mm});
            skPoint(sketch, "E136", {"position": v(15.2, 7.2) * mm});
            skLineSegment(sketch, "E137.bottom", {"start": v(15.2, 7.2) * mm, "end": v(-50.8, 7.2) * mm});
            skLineSegment(sketch, "E137.top", {"start": v(15.2, 6.2) * mm, "end": v(-50.8, 6.2) * mm});
            skLineSegment(sketch, "E137.left", {"start": v(15.2, 7.2) * mm, "end": v(15.2, 6.2) * mm});
            skLineSegment(sketch, "E137.right", {"start": v(-50.8, 7.2) * mm, "end": v(-50.8, 6.2) * mm});
            skLineSegment(sketch, "E138.bottom", {"start": v(15.2, 7.2) * mm, "end": v(14.2, 7.2) * mm});
            skLineSegment(sketch, "E138.top", {"start": v(15.2, -14.8) * mm, "end": v(14.2, -14.8) * mm});
            skLineSegment(sketch, "E138.left", {"start": v(15.2, 7.2) * mm, "end": v(15.2, -14.8) * mm});
            skLineSegment(sketch, "E138.right", {"start": v(14.2, 7.2) * mm, "end": v(14.2, -14.8) * mm});
            skPoint(sketch, "E139", {"position": v(47.2, -13.8) * mm});
            skLineSegment(sketch, "E140.bottom", {"start": v(47.2, -13.8) * mm, "end": v(15.2, -13.8) * mm});
            skLineSegment(sketch, "E140.top", {"start": v(47.2, -14.8) * mm, "end": v(15.2, -14.8) * mm});
            skLineSegment(sketch, "E140.left", {"start": v(47.2, -13.8) * mm, "end": v(47.2, -14.8) * mm});
            skLineSegment(sketch, "E140.right", {"start": v(15.2, -13.8) * mm, "end": v(15.2, -14.8) * mm});
            skLineSegment(sketch, "E141.bottom", {"start": v(47.2, -13.8) * mm, "end": v(46.2, -13.8) * mm});
            skLineSegment(sketch, "E141.top", {"start": v(47.2, -33.2) * mm, "end": v(46.2, -33.2) * mm});
            skLineSegment(sketch, "E141.left", {"start": v(47.2, -13.8) * mm, "end": v(47.2, -33.2) * mm});
            skLineSegment(sketch, "E141.right", {"start": v(46.2, -13.8) * mm, "end": v(46.2, -33.2) * mm});
            skPoint(sketch, "E142", {"position": v(56.8, -32.2) * mm});
            skLineSegment(sketch, "E143.bottom", {"start": v(56.8, -32.2) * mm, "end": v(47.2, -32.2) * mm});
            skLineSegment(sketch, "E143.top", {"start": v(56.8, -33.2) * mm, "end": v(47.2, -33.2) * mm});
            skLineSegment(sketch, "E143.left", {"start": v(56.8, -32.2) * mm, "end": v(56.8, -33.2) * mm});
            skLineSegment(sketch, "E143.right", {"start": v(47.2, -32.2) * mm, "end": v(47.2, -33.2) * mm});
            skPoint(sketch, "E144", {"position": v(21.2, 14.8) * mm});
            skPoint(sketch, "E145", {"position": v(22.2, -7.8) * mm});
            skLineSegment(sketch, "E146.bottom", {"start": v(22.2, -7.8) * mm, "end": v(21.2, -7.8) * mm});
            skLineSegment(sketch, "E146.top", {"start": v(22.2, 14.8) * mm, "end": v(21.2, 14.8) * mm});
            skLineSegment(sketch, "E146.left", {"start": v(22.2, -7.8) * mm, "end": v(22.2, 14.8) * mm});
            skLineSegment(sketch, "E146.right", {"start": v(21.2, -7.8) * mm, "end": v(21.2, 14.8) * mm});
            skPoint(sketch, "E147", {"position": v(28.2, 8.8) * mm});
            skPoint(sketch, "E148", {"position": v(29.2, -13.8) * mm});
            skLineSegment(sketch, "E149.bottom", {"start": v(29.2, -13.8) * mm, "end": v(28.2, -13.8) * mm});
            skLineSegment(sketch, "E149.top", {"start": v(29.2, 8.8) * mm, "end": v(28.2, 8.8) * mm});
            skLineSegment(sketch, "E149.left", {"start": v(29.2, -13.8) * mm, "end": v(29.2, 8.8) * mm});
            skLineSegment(sketch, "E149.right", {"start": v(28.2, -13.8) * mm, "end": v(28.2, 8.8) * mm});
            skPoint(sketch, "E150", {"position": v(35.2, -7.8) * mm});
            skPoint(sketch, "E151", {"position": v(36.2, 14.8) * mm});
            skLineSegment(sketch, "E152.bottom", {"start": v(35.2, -7.8) * mm, "end": v(36.2, -7.8) * mm});
            skLineSegment(sketch, "E152.top", {"start": v(35.2, 14.8) * mm, "end": v(36.2, 14.8) * mm});
            skLineSegment(sketch, "E152.left", {"start": v(35.2, -7.8) * mm, "end": v(35.2, 14.8) * mm});
            skLineSegment(sketch, "E152.right", {"start": v(36.2, -7.8) * mm, "end": v(36.2, 14.8) * mm});
            skPoint(sketch, "E153", {"position": v(42.2, 8.8) * mm});
            skPoint(sketch, "E154", {"position": v(43.2, -13.8) * mm});
            skLineSegment(sketch, "E155.bottom", {"start": v(42.2, 8.8) * mm, "end": v(43.2, 8.8) * mm});
            skLineSegment(sketch, "E155.top", {"start": v(42.2, -13.8) * mm, "end": v(43.2, -13.8) * mm});
            skLineSegment(sketch, "E155.left", {"start": v(42.2, 8.8) * mm, "end": v(42.2, -13.8) * mm});
            skLineSegment(sketch, "E155.right", {"start": v(43.2, 8.8) * mm, "end": v(43.2, -13.8) * mm});
            skLineSegment(sketch, "E156.bottom", {"start": v(49.8, 15.8) * mm, "end": v(50.8, 15.8) * mm});
            skLineSegment(sketch, "E156.top", {"start": v(49.8, 1.8) * mm, "end": v(50.8, 1.8) * mm});
            skLineSegment(sketch, "E156.left", {"start": v(49.8, 15.8) * mm, "end": v(49.8, 1.8) * mm});
            skLineSegment(sketch, "E156.right", {"start": v(50.8, 15.8) * mm, "end": v(50.8, 1.8) * mm});
            skPoint(sketch, "E157", {"position": v(43.2, -5.2) * mm});
            skLineSegment(sketch, "E158.bottom", {"start": v(43.2, -5.2) * mm, "end": v(50.8, -5.2) * mm});
            skLineSegment(sketch, "E158.top", {"start": v(43.2, -4.2) * mm, "end": v(50.8, -4.2) * mm});
            skLineSegment(sketch, "E158.left", {"start": v(43.2, -5.2) * mm, "end": v(43.2, -4.2) * mm});
            skLineSegment(sketch, "E159.bottom", {"start": v(-50.8, 7.8) * mm, "end": v(-49.8, 7.8) * mm});
            skLineSegment(sketch, "E159.left", {"start": v(-50.8, 7.8) * mm, "end": v(-50.8, 6.2) * mm});
            skLineSegment(sketch, "E159.right", {"start": v(-49.8, 7.8) * mm, "end": v(-49.8, 6.2) * mm});
            skSolve(sketch);
        }
        {
            var Q0;
            {var subQ1=sQuery(id+"F6.wireOp",EDGE,"E104.left");Q0=makeQuery(id+"F6.imprint","IMPRINT",FACE,{"disambiguationData":[TD([[makeQuery(id+"F6.imprint","IMPRINT",EDGE,{"derivedFrom":subQ1}),1.0]])]});}
            var Q1;
            {var subQ18=sQuery(id+"F6.wireOp",EDGE,"E102.left");Q1=makeQuery(id+"F6.imprint","IMPRINT",FACE,{"disambiguationData":[TD([[makeQuery(id+"F6.imprint","IMPRINT",EDGE,{"derivedFrom":subQ18}),-1.0]])]});}
            var Q2;
            {var subQ9=sQuery(id+"F6.wireOp",EDGE,"E102.right");Q2=makeQuery(id+"F6.imprint","IMPRINT",FACE,{"disambiguationData":[TD([[makeQuery(id+"F6.imprint","IMPRINT",EDGE,{"derivedFrom":subQ9}),1.0]])]});}
            var Q3;
            {var subQ6=sQuery(id+"F6.wireOp",EDGE,"E132.bottom");Q3=makeQuery(id+"F6.imprint","IMPRINT",FACE,{"disambiguationData":[TD([[makeQuery(id+"F6.imprint","IMPRINT",EDGE,{"derivedFrom":subQ6}),-1.0]])]});}
            extrude(context, id + "F7", {"entities" : qUnion([Q0, Q1, Q2, Q3]), "operationType" : NewBodyOperationType.REMOVE, "oppositeDirection" : true, "depth" : 6 * mm, "offsetDistance" : 25.4 * mm});
        }
        {
            var Q0;
            Q0=makeQuery(id+"F7.boolean.opBoolean","COPY",FACE,{"derivedFrom":makeQuery(id+"F7.opExtrude","CAP_FACE",FACE,{"disambiguationData":[OSD([sQuery(id+"F0.wireOp",EDGE,"E0.bottom"),sQuery(id+"F0.wireOp",EDGE,"E0.right"),sQuery(id+"F6.wireOp",EDGE,"E104.left"),sQuery(id+"F6.wireOp",EDGE,"E106.right"),sQuery(id+"F6.wireOp",EDGE,"E116.left"),sQuery(id+"F6.wireOp",EDGE,"E124.right"),sQuery(id+"F6.wireOp",EDGE,"E133.top"),sQuery(id+"F6.wireOp",EDGE,"E135.left"),sQuery(id+"F6.wireOp",EDGE,"E159.left")])],"isStart":false})});
            extrude(context, id + "F8", {"entities" : qUnion([Q0]), "operationType" : NewBodyOperationType.REMOVE, "oppositeDirection" : true, "depth" : 25.4 * mm, "offsetDistance" : 25.4 * mm});
        }
        {
            var Q0;
            {var subQ0=sQuery(id+"F2.wireOp",EDGE,"E41.right");Q0=makeQuery(id+"F5.boolean.opBoolean","MERGE",FACE,{"derivedFrom":[makeQuery(id+"F3.boolean.opBoolean","COPY",FACE,{"derivedFrom":makeQuery(id+"F3.opExtrude","CAP_FACE",FACE,{"disambiguationData":[OSD([sQuery(id+"F0.wireOp",EDGE,"E0.top"),sQuery(id+"F0.wireOp",EDGE,"E0.right"),sQuery(id+"F2.wireOp",EDGE,"E3.bottom"),sQuery(id+"F2.wireOp",EDGE,"E3.top"),sQuery(id+"F2.wireOp",EDGE,"E6.bottom"),sQuery(id+"F2.wireOp",EDGE,"E8.right"),sQuery(id+"F2.wireOp",EDGE,"E10.left"),sQuery(id+"F2.wireOp",EDGE,"E10.right"),sQuery(id+"F2.wireOp",EDGE,"E12.bottom"),sQuery(id+"F2.wireOp",EDGE,"E12.top"),sQuery(id+"F2.wireOp",EDGE,"E12.left"),sQuery(id+"F2.wireOp",EDGE,"E15.bottom"),sQuery(id+"F2.wireOp",EDGE,"E15.top"),sQuery(id+"F2.wireOp",EDGE,"E15.left"),sQuery(id+"F2.wireOp",EDGE,"E18.bottom"),sQuery(id+"F2.wireOp",EDGE,"E18.top"),sQuery(id+"F2.wireOp",EDGE,"E18.right"),sQuery(id+"F2.wireOp",EDGE,"E20.bottom"),sQuery(id+"F2.wireOp",EDGE,"E20.top"),sQuery(id+"F2.wireOp",EDGE,"E20.left"),sQuery(id+"F2.wireOp",EDGE,"E23.bottom"),sQuery(id+"F2.wireOp",EDGE,"E23.top"),sQuery(id+"F2.wireOp",EDGE,"E23.right"),sQuery(id+"F2.wireOp",EDGE,"E28.bottom"),sQuery(id+"F2.wireOp",EDGE,"E28.top"),sQuery(id+"F2.wireOp",EDGE,"E28.left"),sQuery(id+"F2.wireOp",EDGE,"E30.top"),sQuery(id+"F2.wireOp",EDGE,"E32.bottom"),sQuery(id+"F2.wireOp",EDGE,"E32.top"),sQuery(id+"F2.wireOp",EDGE,"E34.bottom"),sQuery(id+"F2.wireOp",EDGE,"E34.right"),sQuery(id+"F2.wireOp",EDGE,"E36.bottom"),sQuery(id+"F2.wireOp",EDGE,"E36.top"),sQuery(id+"F2.wireOp",EDGE,"E36.left"),sQuery(id+"F2.wireOp",EDGE,"E36.right"),sQuery(id+"F2.wireOp",EDGE,"E38.bottom"),subQ0,sQuery(id+"F2.wireOp",EDGE,"E43.bottom"),sQuery(id+"F2.wireOp",EDGE,"E45.top"),sQuery(id+"F2.wireOp",EDGE,"E45.left"),sQuery(id+"F2.wireOp",EDGE,"E47.bottom"),sQuery(id+"F2.wireOp",EDGE,"E47.top"),sQuery(id+"F2.wireOp",EDGE,"E47.left"),sQuery(id+"F2.wireOp",EDGE,"E49.bottom"),sQuery(id+"F2.wireOp",EDGE,"E49.left"),sQuery(id+"F2.wireOp",EDGE,"E49.right"),sQuery(id+"F2.wireOp",EDGE,"E51.bottom"),sQuery(id+"F2.wireOp",EDGE,"E51.top"),sQuery(id+"F2.wireOp",EDGE,"E53.left"),sQuery(id+"F2.wireOp",EDGE,"E53.right"),sQuery(id+"F2.wireOp",EDGE,"E54.left"),sQuery(id+"F2.wireOp",EDGE,"E54.right"),sQuery(id+"F2.wireOp",EDGE,"E56.bottom"),sQuery(id+"F2.wireOp",EDGE,"E56.top"),sQuery(id+"F2.wireOp",EDGE,"E56.left"),sQuery(id+"F2.wireOp",EDGE,"E56.right"),sQuery(id+"F2.wireOp",EDGE,"E59.bottom"),sQuery(id+"F2.wireOp",EDGE,"E59.top"),sQuery(id+"F2.wireOp",EDGE,"E59.left"),sQuery(id+"F2.wireOp",EDGE,"E62.bottom"),sQuery(id+"F2.wireOp",EDGE,"E62.top"),sQuery(id+"F2.wireOp",EDGE,"E62.right"),sQuery(id+"F2.wireOp",EDGE,"E64.bottom"),sQuery(id+"F2.wireOp",EDGE,"E64.top"),sQuery(id+"F2.wireOp",EDGE,"E64.left"),sQuery(id+"F2.wireOp",EDGE,"E66.bottom"),sQuery(id+"F2.wireOp",EDGE,"E66.top"),sQuery(id+"F2.wireOp",EDGE,"E66.left"),sQuery(id+"F2.wireOp",EDGE,"E69.bottom"),sQuery(id+"F2.wireOp",EDGE,"E69.left"),sQuery(id+"F2.wireOp",EDGE,"E69.right"),sQuery(id+"F2.wireOp",EDGE,"E71.bottom"),sQuery(id+"F2.wireOp",EDGE,"E71.top"),sQuery(id+"F2.wireOp",EDGE,"E71.left"),sQuery(id+"F2.wireOp",EDGE,"E74.bottom"),sQuery(id+"F2.wireOp",EDGE,"E74.right"),sQuery(id+"F2.wireOp",EDGE,"E76.top")])],"isStart":false})}),makeQuery(id+"F5.opExtrude","CAP_FACE",FACE,{"disambiguationData":[OSD([sQuery(id+"F0.wireOp",EDGE,"E0.left"),subQ0,sQuery(id+"F4.wireOp",EDGE,"E83.right"),sQuery(id+"F4.wireOp",EDGE,"E86.bottom"),sQuery(id+"F4.wireOp",EDGE,"E92.top"),sQuery(id+"F4.wireOp",EDGE,"E94.bottom"),sQuery(id+"F4.wireOp",EDGE,"E94.left"),sQuery(id+"F4.wireOp",EDGE,"E96.left"),sQuery(id+"F4.wireOp",EDGE,"E97.bottom"),sQuery(id+"F4.wireOp",EDGE,"E97.right")])],"isStart":false})]});}
            var sketch = newSketch(context, id + "F9", { "sketchPlane" : qUnion([Q0])});
            skPoint(sketch, "E160", {"position": v(-50.8, -38.16) * mm});
            skLineSegment(sketch, "E161", {"start": v(-50.8, -38.16) * mm, "end": v(-50.8, -41.8) * mm});
            skLineSegment(sketch, "E162", {"start": v(-50.8, -41.8) * mm, "end": v(-50.8, -34.8) * mm});
            skPoint(sketch, "E163", {"position": v(-50.8, -48.8) * mm});
            skLineSegment(sketch, "E164", {"start": v(-50.8, -48.8) * mm, "end": v(-50.8, -42.8) * mm});
            skPoint(sketch, "E165", {"position": v(50.8, -33.2) * mm});
            skLineSegment(sketch, "E166", {"start": v(50.8, -33.2) * mm, "end": v(50.8, -39.2) * mm});
            skLineSegment(sketch, "E167", {"start": v(-50.8, -48.8) * mm, "end": v(-50.8, -50.63) * mm});
            skPoint(sketch, "E168", {"position": v(-50.8, -50.8) * mm});
            skLineSegment(sketch, "E169", {"start": v(-50.8, -50.63) * mm, "end": v(-50.8, -48.8) * mm});
            skPoint(sketch, "E170", {"position": v(-56.8, -49.83) * mm});
            skLineSegment(sketch, "E171.bottom", {"start": v(-56.8, -49.83) * mm, "end": v(-50.8, -49.83) * mm});
            skLineSegment(sketch, "E171.top", {"start": v(-56.8, -50.63) * mm, "end": v(-50.8, -50.63) * mm});
            skLineSegment(sketch, "E171.left", {"start": v(-56.8, -49.83) * mm, "end": v(-56.8, -50.63) * mm});
            skLineSegment(sketch, "E171.right", {"start": v(-50.8, -49.83) * mm, "end": v(-50.8, -50.63) * mm});
            skSolve(sketch);
        }
        {
            var Q0;
            Q0=makeQuery(id+"F3.boolean.opBoolean","COPY",FACE,{"derivedFrom":makeQuery(id+"F3.opExtrude","CAP_FACE",FACE,{"disambiguationData":[OSD([sQuery(id+"F0.wireOp",EDGE,"E0.top"),sQuery(id+"F0.wireOp",EDGE,"E0.right"),sQuery(id+"F2.wireOp",EDGE,"E74.left"),sQuery(id+"F2.wireOp",EDGE,"E76.bottom")])],"isStart":false})});
            extrude(context, id + "F10", {"entities" : qUnion([Q0]), "operationType" : NewBodyOperationType.ADD, "depth" : 6 * mm, "offsetDistance" : 25.4 * mm});
        }
        {
            var Q0;
            {var subQ0=sQuery(id+"F2.wireOp",EDGE,"E3.top");var subQ1=sQuery(id+"F0.wireOp",EDGE,"E0.right");var subQ2=makeQuery(id+"F1.opExtrude","CAP_EDGE",EDGE,{"disambiguationData":[OSD([subQ1])],"isStart":false});var subQ4=makeQuery(id+"F3.boolean.opBoolean","COPY",EDGE,{"derivedFrom":makeQuery(id+"F3.opExtrude","CAP_EDGE",EDGE,{"disambiguationData":[OSD([subQ1]),TDD([makeQuery(id+"F2.imprint","IMPRINT",EDGE,{"disambiguationData":[TD([[makeQuery(id+"F2.imprint","INTERSECT",VERTEX,{"derivedFrom":[subQ2,subQ0,sQuery(id+"F2.wireOp",EDGE,"E3.left")]}),1.0]])],"derivedFrom":subQ2})])],"isStart":false})});Q0=makeQuery(id+"F9.imprint","IMPRINT",FACE,{"disambiguationData":[TD([[makeQuery(id+"F9.imprint","IMPRINT",EDGE,{"derivedFrom":subQ4}),1.0]])]});}
            var Q1;
            {var subQ0=sQuery(id+"F9.wireOp",EDGE,"E164");Q1=makeQuery(id+"F9.imprint","IMPRINT",FACE,{"disambiguationData":[TD([[makeQuery(id+"F9.imprint","IMPRINT",EDGE,{"derivedFrom":subQ0}),1.0]])]});}
            var Q2;
            {var subQ0=sQuery(id+"F9.wireOp",EDGE,"E166");Q2=makeQuery(id+"F9.imprint","IMPRINT",FACE,{"disambiguationData":[TD([[makeQuery(id+"F9.imprint","IMPRINT",EDGE,{"derivedFrom":subQ0}),1.0]])]});}
            extrude(context, id + "F11", {"entities" : qUnion([Q0, Q1, Q2]), "operationType" : NewBodyOperationType.REMOVE, "oppositeDirection" : true, "depth" : 25.4 * mm, "offsetDistance" : 25.4 * mm});
        }
        {
            var Q0;
            Q0=makeQuery(id+"F7.boolean.opBoolean","COPY",FACE,{"derivedFrom":makeQuery(id+"F7.opExtrude","CAP_FACE",FACE,{"disambiguationData":[OSD([sQuery(id+"F0.wireOp",EDGE,"E0.left"),sQuery(id+"F6.wireOp",EDGE,"E132.bottom"),sQuery(id+"F6.wireOp",EDGE,"E140.bottom"),sQuery(id+"F6.wireOp",EDGE,"E141.bottom"),sQuery(id+"F6.wireOp",EDGE,"E141.left"),sQuery(id+"F6.wireOp",EDGE,"E143.bottom"),sQuery(id+"F6.wireOp",EDGE,"E155.right"),sQuery(id+"F6.wireOp",EDGE,"E158.bottom")])],"isStart":false})});
            var sketch = newSketch(context, id + "F12", { "sketchPlane" : qUnion([Q0])});
            skPoint(sketch, "E172", {"position": v(50.8, -16.54) * mm});
            skLineSegment(sketch, "E173", {"start": v(50.8, -16.54) * mm, "end": v(50.8, -5.2) * mm});
            skLineSegment(sketch, "E174", {"start": v(50.8, -5.2) * mm, "end": v(50.8, -32.2) * mm});
            skPoint(sketch, "E174.endSnap0", {"position": v(50.8, -10.87) * mm});
            skSolve(sketch);
        }
        {
            var Q0;
            {var subQ7=sQuery(id+"F12.wireOp",EDGE,"E174");var subQ11=makeQuery(id+"F12.imprint","IMPRINT",VERTEX,{"derivedFrom":subQ7});Q0=makeQuery(id+"F12.imprint","IMPRINT",FACE,{"disambiguationData":[TD([[makeQuery(id+"F12.imprint","IMPRINT",EDGE,{"disambiguationData":[TD([[subQ11,-1.0]])],"derivedFrom":subQ7}),1.0]])]});}
            extrude(context, id + "F13", {"entities" : qUnion([Q0]), "operationType" : NewBodyOperationType.REMOVE, "oppositeDirection" : true, "depth" : 25.4 * mm, "offsetDistance" : 25.4 * mm});
        }
        {
            var Q0;
            Q0=makeQuery(id+"F7.boolean.opBoolean","COPY",FACE,{"derivedFrom":makeQuery(id+"F7.opExtrude","CAP_FACE",FACE,{"disambiguationData":[OSD([sQuery(id+"F0.wireOp",EDGE,"E0.bottom"),sQuery(id+"F0.wireOp",EDGE,"E0.left"),sQuery(id+"F6.wireOp",EDGE,"E102.left"),sQuery(id+"F6.wireOp",EDGE,"E104.bottom"),sQuery(id+"F6.wireOp",EDGE,"E104.right"),sQuery(id+"F6.wireOp",EDGE,"E106.left"),sQuery(id+"F6.wireOp",EDGE,"E108.bottom"),sQuery(id+"F6.wireOp",EDGE,"E108.top"),sQuery(id+"F6.wireOp",EDGE,"E108.left"),sQuery(id+"F6.wireOp",EDGE,"E110.top"),sQuery(id+"F6.wireOp",EDGE,"E112.left"),sQuery(id+"F6.wireOp",EDGE,"E114.bottom"),sQuery(id+"F6.wireOp",EDGE,"E114.top"),sQuery(id+"F6.wireOp",EDGE,"E114.left"),sQuery(id+"F6.wireOp",EDGE,"E116.right"),sQuery(id+"F6.wireOp",EDGE,"E118.bottom"),sQuery(id+"F6.wireOp",EDGE,"E118.top"),sQuery(id+"F6.wireOp",EDGE,"E118.left"),sQuery(id+"F6.wireOp",EDGE,"E120.left"),sQuery(id+"F6.wireOp",EDGE,"E122.bottom"),sQuery(id+"F6.wireOp",EDGE,"E122.top"),sQuery(id+"F6.wireOp",EDGE,"E122.left"),sQuery(id+"F6.wireOp",EDGE,"E124.left"),sQuery(id+"F6.wireOp",EDGE,"E126.bottom"),sQuery(id+"F6.wireOp",EDGE,"E126.top"),sQuery(id+"F6.wireOp",EDGE,"E126.left"),sQuery(id+"F6.wireOp",EDGE,"E129.bottom"),sQuery(id+"F6.wireOp",EDGE,"E132.top"),sQuery(id+"F6.wireOp",EDGE,"E137.bottom"),sQuery(id+"F6.wireOp",EDGE,"E138.bottom"),sQuery(id+"F6.wireOp",EDGE,"E138.left"),sQuery(id+"F6.wireOp",EDGE,"E140.bottom"),sQuery(id+"F6.wireOp",EDGE,"E146.bottom"),sQuery(id+"F6.wireOp",EDGE,"E146.left"),sQuery(id+"F6.wireOp",EDGE,"E146.right"),sQuery(id+"F6.wireOp",EDGE,"E149.top"),sQuery(id+"F6.wireOp",EDGE,"E149.left"),sQuery(id+"F6.wireOp",EDGE,"E149.right"),sQuery(id+"F6.wireOp",EDGE,"E152.bottom"),sQuery(id+"F6.wireOp",EDGE,"E152.left"),sQuery(id+"F6.wireOp",EDGE,"E152.right"),sQuery(id+"F6.wireOp",EDGE,"E155.bottom"),sQuery(id+"F6.wireOp",EDGE,"E155.left"),sQuery(id+"F6.wireOp",EDGE,"E155.right"),sQuery(id+"F6.wireOp",EDGE,"E156.top"),sQuery(id+"F6.wireOp",EDGE,"E156.left"),sQuery(id+"F6.wireOp",EDGE,"E158.top"),sQuery(id+"F6.wireOp",EDGE,"E159.right")])],"isStart":false})});
            var sketch = newSketch(context, id + "F14", { "sketchPlane" : qUnion([Q0])});
            skPoint(sketch, "E175", {"position": v(50.8, -4.2) * mm});
            skLineSegment(sketch, "E176", {"start": v(50.8, -4.2) * mm, "end": v(50.8, 1.8) * mm});
            skSolve(sketch);
        }
        {
            var Q0;
            {var subQ0=sQuery(id+"F14.wireOp",EDGE,"E176");Q0=makeQuery(id+"F14.imprint","IMPRINT",FACE,{"disambiguationData":[TD([[makeQuery(id+"F14.imprint","IMPRINT",EDGE,{"derivedFrom":subQ0}),-1.0]])]});}
            extrude(context, id + "F15", {"entities" : qUnion([Q0]), "operationType" : NewBodyOperationType.REMOVE, "oppositeDirection" : true, "depth" : 25.4 * mm, "offsetDistance" : 25.4 * mm});
        }
        {
            var Q0;
            Q0=makeQuery(id+"F7.boolean.opBoolean","COPY",FACE,{"derivedFrom":makeQuery(id+"F7.opExtrude","CAP_FACE",FACE,{"disambiguationData":[OSD([sQuery(id+"F0.wireOp",EDGE,"E0.bottom"),sQuery(id+"F0.wireOp",EDGE,"E0.left"),sQuery(id+"F6.wireOp",EDGE,"E102.right"),sQuery(id+"F6.wireOp",EDGE,"E110.bottom"),sQuery(id+"F6.wireOp",EDGE,"E112.top"),sQuery(id+"F6.wireOp",EDGE,"E112.right"),sQuery(id+"F6.wireOp",EDGE,"E118.right"),sQuery(id+"F6.wireOp",EDGE,"E120.right"),sQuery(id+"F6.wireOp",EDGE,"E129.top"),sQuery(id+"F6.wireOp",EDGE,"E156.right")])],"isStart":false})});
            var sketch = newSketch(context, id + "F16", { "sketchPlane" : qUnion([Q0])});
            skLineSegment(sketch, "E177", {"start": v(50.8, 43.8) * mm, "end": v(50.8, 50.8) * mm});
            skSolve(sketch);
        }
        {
            var Q0;
            {var subQ7=sQuery(id+"F16.wireOp",EDGE,"E177");Q0=makeQuery(id+"F16.imprint","IMPRINT",FACE,{"disambiguationData":[TD([[makeQuery(id+"F16.imprint","IMPRINT",EDGE,{"derivedFrom":subQ7}),-1.0]])]});}
            extrude(context, id + "F17", {"entities" : qUnion([Q0]), "operationType" : NewBodyOperationType.REMOVE, "oppositeDirection" : true, "depth" : 25.4 * mm, "offsetDistance" : 25.4 * mm});
        }
        {
            var Q0;
            Q0=makeQuery(id+"F5.boolean.opBoolean","COPY",FACE,{"derivedFrom":makeQuery(id+"F5.opExtrude","CAP_FACE",FACE,{"disambiguationData":[OSD([sQuery(id+"F0.wireOp",EDGE,"E0.top"),sQuery(id+"F0.wireOp",EDGE,"E0.left"),sQuery(id+"F4.wireOp",EDGE,"E78.right"),sQuery(id+"F4.wireOp",EDGE,"E80.left"),sQuery(id+"F4.wireOp",EDGE,"E86.top"),sQuery(id+"F4.wireOp",EDGE,"E88.bottom"),sQuery(id+"F4.wireOp",EDGE,"E89.bottom"),sQuery(id+"F4.wireOp",EDGE,"E89.left")])],"isStart":false})});
            var sketch = newSketch(context, id + "F18", { "sketchPlane" : qUnion([Q0])});
            skPoint(sketch, "E178", {"position": v(50.8, -50.8) * mm});
            skLineSegment(sketch, "E179", {"start": v(50.8, -50.8) * mm, "end": v(50.8, -40.2) * mm});
            skSolve(sketch);
        }
        {
            var Q0;
            {var subQ0=sQuery(id+"F18.wireOp",EDGE,"E179");Q0=makeQuery(id+"F18.imprint","IMPRINT",FACE,{"disambiguationData":[TD([[makeQuery(id+"F18.imprint","IMPRINT",EDGE,{"derivedFrom":subQ0}),-1.0]])]});}
            extrude(context, id + "F19", {"entities" : qUnion([Q0]), "operationType" : NewBodyOperationType.REMOVE, "oppositeDirection" : true, "depth" : 25.4 * mm, "offsetDistance" : 25.4 * mm});
        }
    });
